FCSTD DOCUMENT  (FreeCAD 0.20R29177 +426 (Git))
Label: 4-linkage
License: All rights reserved
LicenseURL: http://en.wikipedia.org/wiki/All_rights_reserved
objects: Sketcher::SketchObject×2, PartDesign::Body×2
note: 4 computed .brp shape members not serialized (recipe doc carries the construction recipe); baked Part::Feature solids carry a one-line shape summary decoded from their .brp

FEATURE [Sketcher::SketchObject] Sketch
  FullyConstrained = false
  MapMode = 5
  Support = -> [XY_Plane]
  sketch-geometry (2):
    g0: LineSegment StartX=-119.33 StartY=19.757 StartZ=0 EndX=-90.503 EndY=71.4475 EndZ=0
    g1: LineSegment StartX=-90.503 StartY=71.4475 StartZ=0 EndX=-53.3938 EndY=38.4992 EndZ=0
  constraints (1):
    c: Coincident(g1,g0)
FEATURE [PartDesign::Body] Body
  Group = -> [Sketch]
  Origin = -> Origin
FEATURE [Sketcher::SketchObject] Sketch001
  FullyConstrained = false
  MapMode = 5
  Support = -> [XY_Plane001]
  sketch-geometry (4):
    g0: LineSegment StartX=0 StartY=41.22 StartZ=0 EndX=53.4721 EndY=70.8651 EndZ=0
    g1: LineSegment StartX=0 StartY=0 StartZ=0 EndX=62.4258 EndY=14.5626 EndZ=0
    g2: LineSegment StartX=53.4721 StartY=70.8651 StartZ=0 EndX=62.4258 EndY=14.5626 EndZ=0
    g3: LineSegment StartX=0 StartY=0 StartZ=0 EndX=0 EndY=41.22 EndZ=0
  constraints (9):
    c: Distance(g0) = 61.14
    c: Coincident(g2,g0)
    c: Coincident(g2,g1)
    c: Coincident(g-1,g1)
    c: Coincident(g3,g1)
    c: Vertical(g3)
    c: DistanceY(g3,g3) = 41.22
    c: Coincident(g3,g0)
    c: Distance(g2) = 57.01
FEATURE [PartDesign::Body] Body001
  Group = -> [Sketch001]
  Origin = -> Origin001
